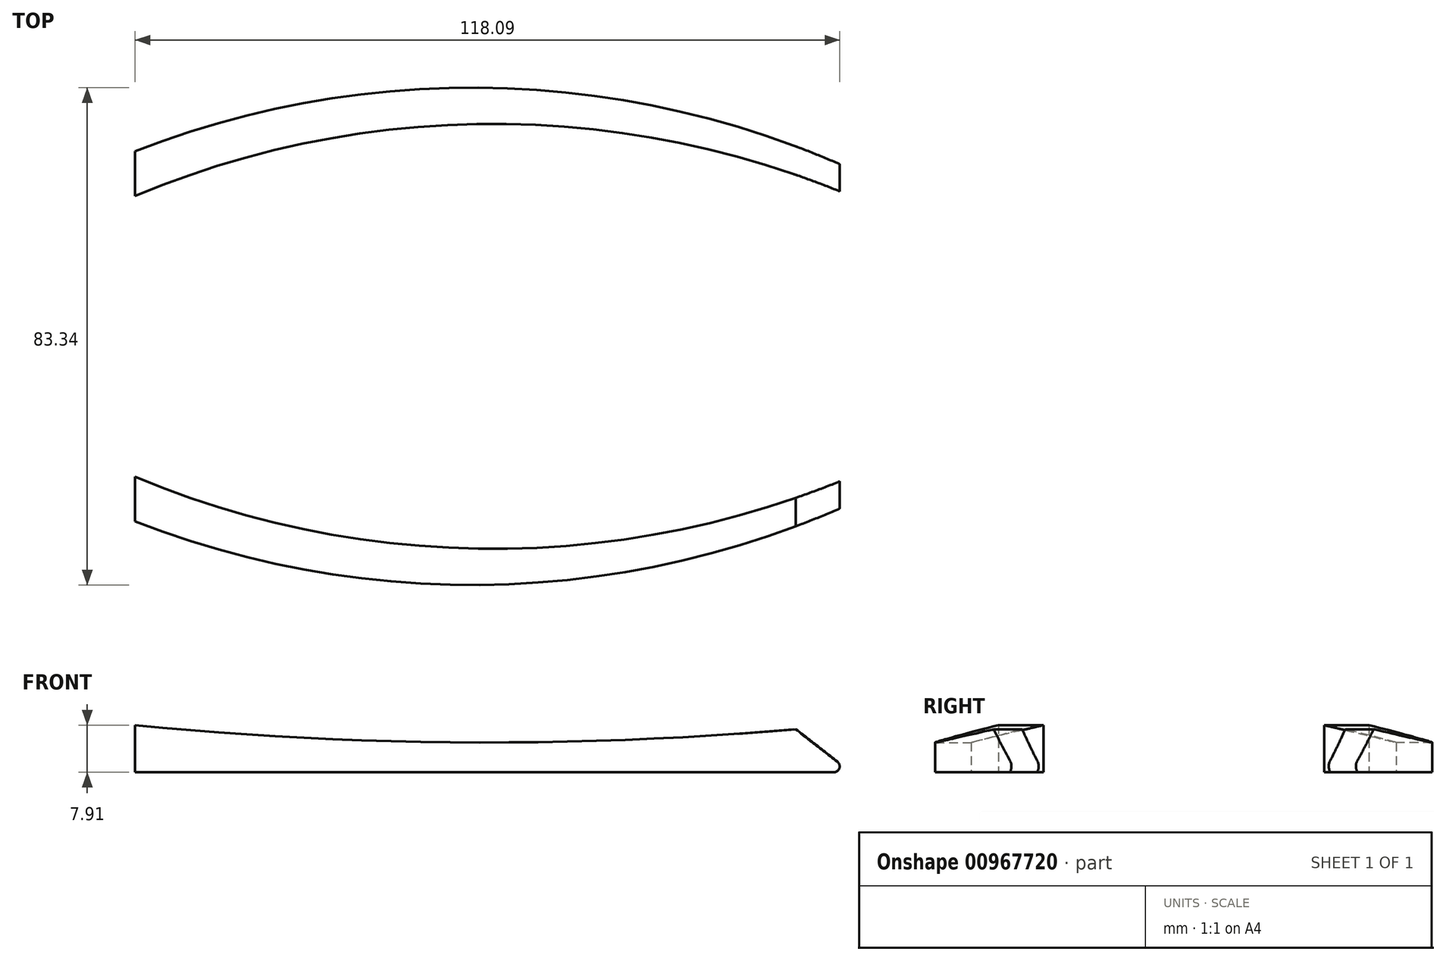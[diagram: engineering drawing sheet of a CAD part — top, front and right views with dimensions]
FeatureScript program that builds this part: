
annotation { "Feature Type Name" : "Feature", "Feature Type Description" : "" }
export const myFeature = defineFeature(function(context is Context, id is Id, definition is map)
    precondition{}
    {
        {
            var Q0;
            Q0=qCreatedBy(makeId("Top.planeOp"),FACE);
            var sketch = newSketch(context, id + "F0", { "sketchPlane" : qUnion([Q0])});
            skArc(sketch, "E0", {"start": v(60, 23.53) * mm, "mid": v(0, 35.61) * mm, "end": v(-60, 23.53) * mm});
            skLineSegment(sketch, "E1", {"start": v(-60, 23.53) * mm, "end": v(60, 23.53) * mm, "construction": true});
            skLineSegment(sketch, "E2", {"start": v(0, 23.53) * mm, "end": v(0, 0) * mm, "construction": true});
            skArc(sketch, "E3", {"start": v(60, 28.03) * mm, "mid": v(0.3, 41.62) * mm, "end": v(-60, 31.03) * mm});
            skLineSegment(sketch, "E4", {"start": v(-60, 31.03) * mm, "end": v(-60, 23.53) * mm});
            skLineSegment(sketch, "E5", {"start": v(60, 28.03) * mm, "end": v(60, 23.53) * mm});
            skSolve(sketch);
        }
        {
            var Q0;
            Q0 = qSketchRegion(id + "F0", true);
            extrude(context, id + "F1", {"entities" : qUnion([Q0]), "depth" : 8 * mm, "offsetDistance" : 25 * mm});
        }
        {
            var Q0;
            Q0=qCreatedBy(makeId("Front.planeOp"),FACE);
            var sketch = newSketch(context, id + "F2", { "sketchPlane" : qUnion([Q0])});
            skArc(sketch, "E6", {"start": v(-60.92, 8) * mm, "mid": v(-0.92, 5) * mm, "end": v(59.08, 8) * mm});
            skLineSegment(sketch, "E7", {"start": v(0, 5) * mm, "end": v(0, 0) * mm, "construction": true});
            skLineSegment(sketch, "E8", {"start": v(-60.92, 8) * mm, "end": v(59.08, 8) * mm});
            skSolve(sketch);
        }
        {
            var Q0;
            Q0 = qSketchRegion(id + "F2", true);
            extrude(context, id + "F3", {"entities" : qUnion([Q0]), "operationType" : NewBodyOperationType.REMOVE, "oppositeDirection" : true, "depth" : 100 * mm, "offsetDistance" : 25 * mm});
        }
        {
            var Q0;
            Q0=makeQuery(id+"F1.opExtrude","CAP_EDGE",EDGE,{"disambiguationData":[OSD([sQuery(id+"F0.wireOp",EDGE,"E5")])],"isStart":false});
            chamfer(context, id + "F4", {"entities" : qUnion([Q0]), "chamferType" : ChamferType.OFFSET_ANGLE, "width" : 7.25 * mm, "oppositeDirection" : false, "angle" : 50 * degree, "tangentPropagation" : true});
        }
        {
            var Q0;
            Q0=makeQuery(id+"F1.opExtrude","SWEPT_BODY",BODY,{"disambiguationData":[OSD([sQuery(id+"F0.wireOp",EDGE,"E0"),sQuery(id+"F0.wireOp",EDGE,"E3"),sQuery(id+"F0.wireOp",EDGE,"E4"),sQuery(id+"F0.wireOp",EDGE,"E5")])]});
            var Q1;
            Q1=qCreatedBy(makeId("Front.planeOp"),FACE);
            mirror(context, id + "F5", {"entities" : qUnion([Q0]), "mirrorPlane" : qUnion([Q1])});
        }
        {
            var Q0;
            {var subQ0=sQuery(id+"F0.wireOp",EDGE,"E5");Q0=makeQuery(id+"F4.opChamfer","BLEND_EDGE",EDGE,{"blendedFrom":[makeQuery(id+"F1.opExtrude","CAP_EDGE",EDGE,{"disambiguationData":[OSD([subQ0])],"isStart":false}),makeQuery(id+"F1.opExtrude","CAP_FACE",FACE,{"disambiguationData":[OSD([sQuery(id+"F0.wireOp",EDGE,"E0"),sQuery(id+"F0.wireOp",EDGE,"E3"),sQuery(id+"F0.wireOp",EDGE,"E4"),subQ0])],"isStart":true})],"blendedInto":[makeQuery(id+"F1.opExtrude","CAP_FACE",FACE,{"disambiguationData":[OSD([sQuery(id+"F0.wireOp",EDGE,"E0"),sQuery(id+"F0.wireOp",EDGE,"E3"),sQuery(id+"F0.wireOp",EDGE,"E4"),subQ0])],"isStart":true})]});}
            var Q1;
            {var subQ0=sQuery(id+"F0.wireOp",EDGE,"E5");Q1=makeQuery(id+"F5.opPattern","COPY",EDGE,{"derivedFrom":makeQuery(id+"F4.opChamfer","BLEND_EDGE",EDGE,{"blendedFrom":[makeQuery(id+"F1.opExtrude","CAP_EDGE",EDGE,{"disambiguationData":[OSD([subQ0])],"isStart":false}),makeQuery(id+"F1.opExtrude","CAP_FACE",FACE,{"disambiguationData":[OSD([sQuery(id+"F0.wireOp",EDGE,"E0"),sQuery(id+"F0.wireOp",EDGE,"E3"),sQuery(id+"F0.wireOp",EDGE,"E4"),subQ0])],"isStart":true})],"blendedInto":[makeQuery(id+"F1.opExtrude","CAP_FACE",FACE,{"disambiguationData":[OSD([sQuery(id+"F0.wireOp",EDGE,"E0"),sQuery(id+"F0.wireOp",EDGE,"E3"),sQuery(id+"F0.wireOp",EDGE,"E4"),subQ0])],"isStart":true})]}),"instanceName":"1"});}
            var Q2;
            Q2=makeQuery(id+"F4.opChamfer","BLEND_EDGE",EDGE,{"blendedFrom":[makeQuery(id+"F1.opExtrude","CAP_EDGE",EDGE,{"disambiguationData":[OSD([sQuery(id+"F0.wireOp",EDGE,"E5")])],"isStart":false}),makeQuery(id+"F3.boolean.opBoolean","COPY",FACE,{"derivedFrom":makeQuery(id+"F3.opExtrude","SWEPT_FACE",FACE,{"disambiguationData":[OSD([sQuery(id+"F2.wireOp",EDGE,"E6")])]})})],"blendedInto":[makeQuery(id+"F3.boolean.opBoolean","COPY",FACE,{"derivedFrom":makeQuery(id+"F3.opExtrude","SWEPT_FACE",FACE,{"disambiguationData":[OSD([sQuery(id+"F2.wireOp",EDGE,"E6")])]})})]});
            fillet(context, id + "F6", {"entities" : qUnion([Q0, Q1, Q2]), "radius" : 1 * mm, "tangentPropagation" : true, "allowEdgeOverflow" : false});
        }
    });
